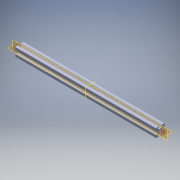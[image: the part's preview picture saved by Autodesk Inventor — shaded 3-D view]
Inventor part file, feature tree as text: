
AUTODESK INVENTOR PART (.ipt)
format: ipt  version: 2018 (Build 220112000, 112)  size: 376,832 bytes
history: native  units: in
note: dims shown in document units (in); Inventor stores cm internally (conversion verified against a paired STEP export)
features: extrude x1, plane x1, sketch x1, projected_geometry x1, fillet x1
ambient origin geometry x8: Origin, YZ Plane, XZ Plane, XY Plane, X Axis, Y Axis, Z Axis, Center Point
bodies: Solid1 (feature_tree)
feature tree (5):
  extrude  "Extrusion2"  [1 undecoded]
  plane  "Work Plane1"
  sketch  "Sketch3"  dims[d2=8.6614in d3=0.0in]
  projected_geometry  "Projected Loop2"
  fillet  "Fillet5"  [1 undecoded]
note: 2 required parameter values undecoded (feature->parameter linkage not recoverable at this tier; creation-order binding heuristic only, values carry confidence <= 0.55)
